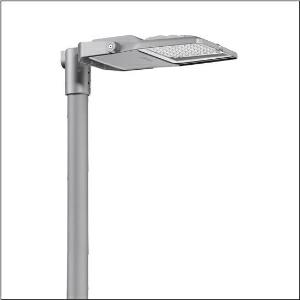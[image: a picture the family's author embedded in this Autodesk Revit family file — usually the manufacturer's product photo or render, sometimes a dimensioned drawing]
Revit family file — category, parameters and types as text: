
# Revit family: floodlight_fl_21_iq_mini___pl52_5xa7772c2d3a_4b1a
name_source: partatom
category: Lighting Fixtures
units: mm (PartAtom-declared; Revit-internal decimal feet)

## family parameters
Cut with Voids When Loaded = No
Host = Face
Light Source = No
Part Type = Normal
Room Calculation Point = No
Round Connector Dimension = Use Diameter
Shared = No

## types (1)
- --- (1 x LED, 12210 lm, 87.2 W, 3000K)
    Apparent Load = 87 VA
    CIE Flux Codes = 26 60 98 100 100
    Color Rendering = 70
    Color Temperature = 3000K
    Default Elevation = 1800 mm
    Description = Floodlight FL 21 iQ mini, floodlight, primary light control with lens, of PMMA, primary optical cover: protective disc, of toughened safety glass, transparent, light distribution: PL52, light emission: direct distribution, installation type: surface-mounted, LED, High Power LED, rated luminous flux: 12.210lm, luminous efficacy: 140lm/W, light colour: 730, colour temperature: 3000K, control: Auto-Match, Temp-Guard, Night-Set, Smart-Wire, Desk-Remote (wireless, voltage-free reading and setting of iQ features in the workshop via application-optimized NFC function/RFID function), optimised constant luminous flux control (CLO 2.0), Light-Fading, Lumen-Switch, with terminal, 6-pole, mains connection: 220..240V, AC, 50/60Hz, start of lifetime: 87W, end of service life: 92W, reduction: 40W, luminaire housing, of diecast aluminium, powder-coated, Siteco® metallic grey (DB 702S), corrosivity category C5 mid according to DIN EN ISO 12944, sealing non-destructively replaceable, please order mast flange separately, mast bracket, of steel, galvanised, powder-coated, protection rating (complete): IP66, insulation class (complete): insulation class II (safety insulation), certification: CE, ENEC, VDE, protection symbol: D, impact resistance: IK08, permissible operating ambient temperature: -40..+40°C, permissible operating ambient temperature for outdoor applications: -40..+50°C, standard: DIN EN 12944, LABS conformity tested according to VDMA 24364:2018-05, packaging unit: 1 piece

Light Distribution: PL52
    Height = 70 mm
    Lamp = 1 x LED
    Lamp Light Flux = 12210 lm
    Lamp Power = 87.2 W
    Lamp count = 1
    Length = 485 mm
    Luminous efficacy = 140 lm/W
    Manufacturer = Siteco
    ModVariant = No
    Model = 5XA7772C2D3A
    Number of Poles = 1
    OnlyDefault = Yes
    Power Factor = 1
    Product Name = Floodlight FL 21 iQ mini | PL52
    Product group = floodlight | pylon annexe
    ProductGroupID = 6200
    Protection Class = Protection class II
    Protection Degree = IP 66
    RLX_Detail_Level = 1
    RLX_Emergency_Light_Flux = 0 lm
    RLX_Emergency_Type = 0
    RLX_Emergency_Type_DB = No
    RlxData = <blob elided: 101525 chars, md5=9e6ad547>
    Socket = socket
    Standby Power = 0 W
    System Light Flux = 12210 lm
    System Power = 87 W
    Type Comments = factory setting: luminous flux: 100 % | dim-lin: 254 | 456 mA
    Type Image = l_1007125.jpg
    URL = http://relux.com
    VarID = @adj_134637
    Voltage = 0 V
    Weight = 0.00 kg
    Width = 337 mm

## geometry (parser evidence)
native form markers: Blend x4, Sweep x14
no freeform markers — native parametric forms only
